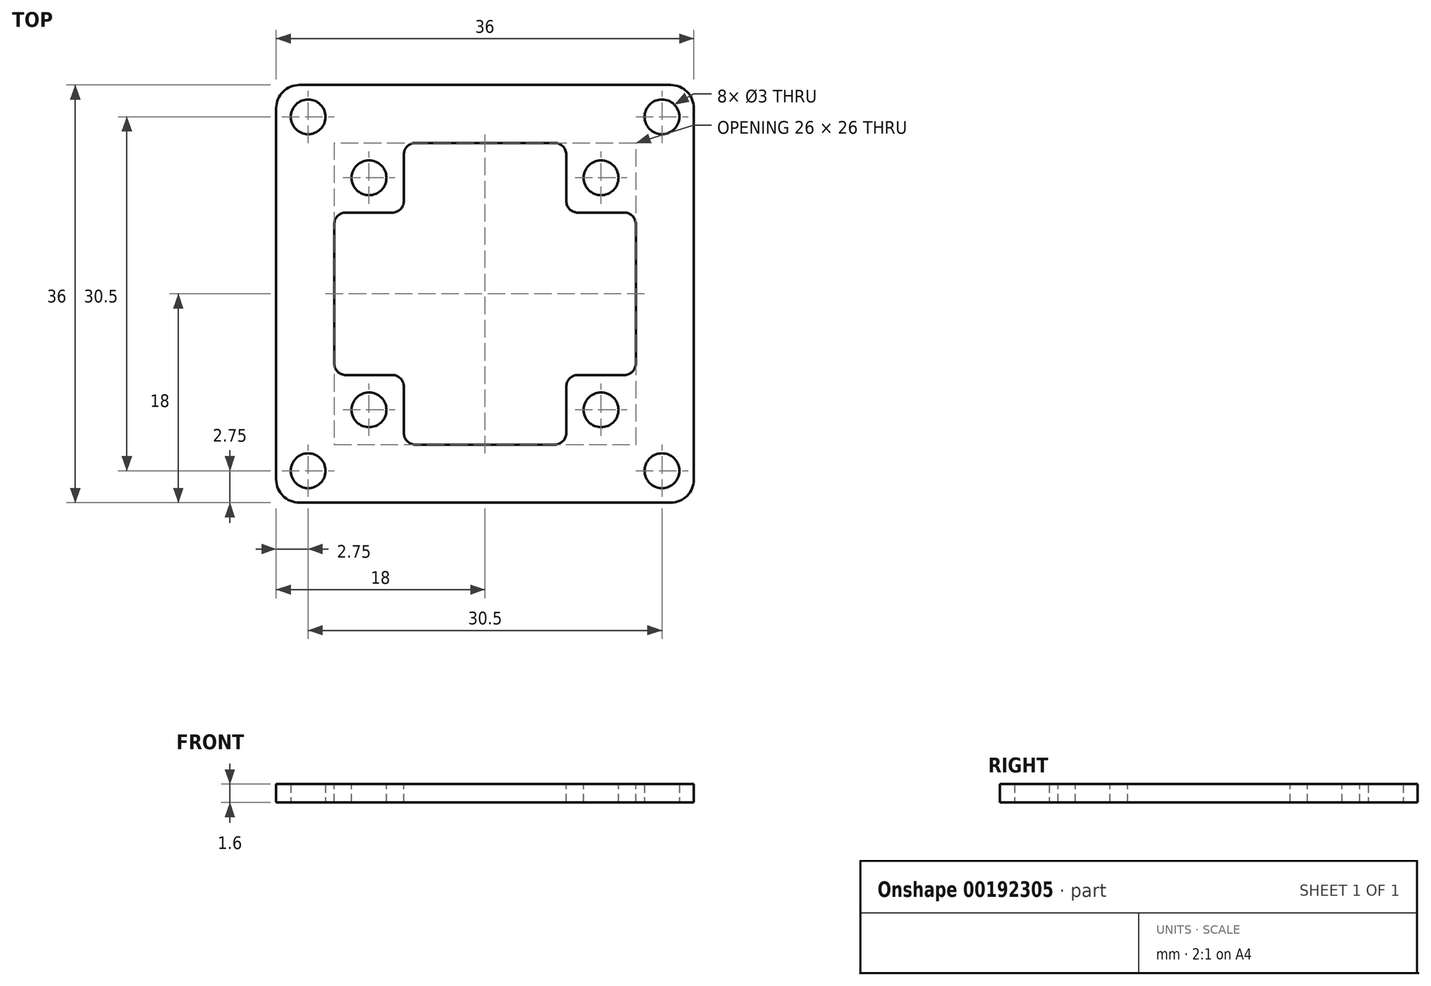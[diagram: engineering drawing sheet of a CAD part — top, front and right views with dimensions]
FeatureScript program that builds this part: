
annotation { "Feature Type Name" : "Feature", "Feature Type Description" : "" }
export const myFeature = defineFeature(function(context is Context, id is Id, definition is map)
    precondition{}
    {
        {
            var Q0;
            Q0=qCreatedBy(makeId("Top.planeOp"),FACE);
            var sketch = newSketch(context, id + "F0", { "sketchPlane" : qUnion([Q0])});
            skLineSegment(sketch, "E0.bottom", {"start": v(0, 0) * mm, "end": v(36, 0) * mm});
            skLineSegment(sketch, "E0.top", {"start": v(0, 36) * mm, "end": v(36, 36) * mm});
            skLineSegment(sketch, "E0.left", {"start": v(0, 0) * mm, "end": v(0, 36) * mm});
            skLineSegment(sketch, "E0.right", {"start": v(36, 0) * mm, "end": v(36, 36) * mm});
            skCircle(sketch, "E1", {"center": v(2.75, 33.25) * mm, "radius": 1.5 * mm});
            skCircle(sketch, "E2", {"center": v(33.25, 33.25) * mm, "radius": 1.5 * mm});
            skCircle(sketch, "E3", {"center": v(33.25, 2.75) * mm, "radius": 1.5 * mm});
            skCircle(sketch, "E4", {"center": v(2.75, 2.75) * mm, "radius": 1.5 * mm});
            skSolve(sketch);
        }
        {
            var Q0;
            Q0=makeQuery(id+"F0.imprint","IMPRINT",FACE,{"disambiguationData":[TD([[makeQuery(id+"F0.imprint","IMPRINT",EDGE,{"derivedFrom":sQuery(id+"F0.wireOp",EDGE,"E0.bottom")}),1.0]])]});
            extrude(context, id + "F1", {"entities" : qUnion([Q0]), "depth" : 1.6 * mm});
        }
        {
            var Q0;
            Q0=makeQuery(id+"F1.opExtrude","SWEPT_EDGE",EDGE,{"disambiguationData":[OSD([sQuery(id+"F0.wireOp",EDGE,"E0.top"),sQuery(id+"F0.wireOp",EDGE,"E0.left")])]});
            var Q1;
            Q1=makeQuery(id+"F1.opExtrude","SWEPT_EDGE",EDGE,{"disambiguationData":[OSD([sQuery(id+"F0.wireOp",EDGE,"E0.top"),sQuery(id+"F0.wireOp",EDGE,"E0.right")])]});
            var Q2;
            Q2=makeQuery(id+"F1.opExtrude","SWEPT_EDGE",EDGE,{"disambiguationData":[OSD([sQuery(id+"F0.wireOp",EDGE,"E0.bottom"),sQuery(id+"F0.wireOp",EDGE,"E0.right")])]});
            var Q3;
            Q3=makeQuery(id+"F1.opExtrude","SWEPT_EDGE",EDGE,{"disambiguationData":[OSD([sQuery(id+"F0.wireOp",EDGE,"E0.bottom"),sQuery(id+"F0.wireOp",EDGE,"E0.left")])]});
            fillet(context, id + "F2", {"entities" : qUnion([Q0, Q1, Q2, Q3]), "radius" : 2 * mm, "tangentPropagation" : true, "allowEdgeOverflow" : false});
        }
        {
            var Q0;
            Q0=makeQuery(id+"F1.opExtrude","CAP_FACE",FACE,{"disambiguationData":[OSD([sQuery(id+"F0.wireOp",EDGE,"E0.bottom"),sQuery(id+"F0.wireOp",EDGE,"E0.top"),sQuery(id+"F0.wireOp",EDGE,"E0.left"),sQuery(id+"F0.wireOp",EDGE,"E0.right"),sQuery(id+"F0.wireOp",EDGE,"E1"),sQuery(id+"F0.wireOp",EDGE,"E2"),sQuery(id+"F0.wireOp",EDGE,"E3"),sQuery(id+"F0.wireOp",EDGE,"E4")])],"isStart":false});
            var sketch = newSketch(context, id + "F3", { "sketchPlane" : qUnion([Q0])});
            skCircle(sketch, "E5", {"center": v(8, 28) * mm, "radius": 1.5 * mm});
            skCircle(sketch, "E6.0.1.0", {"center": v(8, 8) * mm, "radius": 1.5 * mm});
            skCircle(sketch, "E6.1.0.0", {"center": v(28, 28) * mm, "radius": 1.5 * mm});
            skCircle(sketch, "E6.1.1.0", {"center": v(28, 8) * mm, "radius": 1.5 * mm});
            skLineSegment(sketch, "E6.direction1", {"start": v(8, 28) * mm, "end": v(28, 28) * mm, "construction": true});
            skLineSegment(sketch, "E6.direction2", {"start": v(8, 28) * mm, "end": v(8, 8) * mm, "construction": true});
            skSolve(sketch);
        }
        {
            var Q0;
            Q0 = qSketchRegion(id + "F3", true);
            extrude(context, id + "F4", {"entities" : qUnion([Q0]), "operationType" : NewBodyOperationType.REMOVE, "oppositeDirection" : true, "depth" : 25 * mm});
        }
        {
            var Q0;
            Q0=makeQuery(id+"F1.opExtrude","CAP_FACE",FACE,{"disambiguationData":[OSD([sQuery(id+"F0.wireOp",EDGE,"E0.bottom"),sQuery(id+"F0.wireOp",EDGE,"E0.top"),sQuery(id+"F0.wireOp",EDGE,"E0.left"),sQuery(id+"F0.wireOp",EDGE,"E0.right"),sQuery(id+"F0.wireOp",EDGE,"E1"),sQuery(id+"F0.wireOp",EDGE,"E2"),sQuery(id+"F0.wireOp",EDGE,"E3"),sQuery(id+"F0.wireOp",EDGE,"E4")])],"isStart":false});
            var sketch = newSketch(context, id + "F5", { "sketchPlane" : qUnion([Q0])});
            skLineSegment(sketch, "E7.bottom", {"start": v(25, 5) * mm, "end": v(11, 5) * mm});
            skLineSegment(sketch, "E7.top", {"start": v(25, 31) * mm, "end": v(11, 31) * mm});
            skLineSegment(sketch, "E7.left", {"start": v(25, 5) * mm, "end": v(25, 11) * mm});
            skLineSegment(sketch, "E7.right", {"start": v(11, 5) * mm, "end": v(11, 11) * mm});
            skPoint(sketch, "E7.middle", {"position": v(18, 18) * mm});
            skPoint(sketch, "E7.middle.positionSnap0", {"position": v(0, 18) * mm});
            skPoint(sketch, "E7.middle.positionSnap1", {"position": v(18, 0) * mm});
            skPoint(sketch, "E7.centerSnap0", {"position": v(0, 18) * mm});
            skPoint(sketch, "E7.centerSnap1", {"position": v(18, 0) * mm});
            skLineSegment(sketch, "E8.bottom", {"start": v(31, 11) * mm, "end": v(25, 11) * mm});
            skLineSegment(sketch, "E8.top", {"start": v(31, 25) * mm, "end": v(25, 25) * mm});
            skLineSegment(sketch, "E8.left", {"start": v(31, 11) * mm, "end": v(31, 25) * mm});
            skLineSegment(sketch, "E8.right", {"start": v(5, 11) * mm, "end": v(5, 25) * mm});
            skLineSegment(sketch, "E9.trimOffspring", {"start": v(11, 25) * mm, "end": v(5, 25) * mm});
            skLineSegment(sketch, "E10.trimOffspring", {"start": v(11, 25) * mm, "end": v(11, 31) * mm});
            skLineSegment(sketch, "E11.trimOffspring", {"start": v(11, 11) * mm, "end": v(5, 11) * mm});
            skLineSegment(sketch, "E12.trimOffspring", {"start": v(25, 25) * mm, "end": v(25, 31) * mm});
            skSolve(sketch);
        }
        {
            var Q0;
            Q0=makeQuery(id+"F5.imprint","IMPRINT",FACE,{"disambiguationData":[TD([[makeQuery(id+"F5.imprint","IMPRINT",EDGE,{"derivedFrom":sQuery(id+"F5.wireOp",EDGE,"E7.bottom")}),-1.0]])]});
            extrude(context, id + "F6", {"entities" : qUnion([Q0]), "operationType" : NewBodyOperationType.REMOVE, "oppositeDirection" : true, "depth" : 25 * mm});
        }
        {
            var Q0;
            Q0=makeQuery(id+"F6.boolean.opBoolean","COPY",EDGE,{"derivedFrom":makeQuery(id+"F6.opExtrude","SWEPT_EDGE",EDGE,{"disambiguationData":[OSD([sQuery(id+"F5.wireOp",EDGE,"E9.trimOffspring"),sQuery(id+"F5.wireOp",EDGE,"E10.trimOffspring")])]})});
            var Q1;
            Q1=makeQuery(id+"F6.boolean.opBoolean","COPY",EDGE,{"derivedFrom":makeQuery(id+"F6.opExtrude","SWEPT_EDGE",EDGE,{"disambiguationData":[OSD([sQuery(id+"F5.wireOp",EDGE,"E8.top"),sQuery(id+"F5.wireOp",EDGE,"E12.trimOffspring")])]})});
            var Q2;
            Q2=makeQuery(id+"F6.boolean.opBoolean","COPY",EDGE,{"derivedFrom":makeQuery(id+"F6.opExtrude","SWEPT_EDGE",EDGE,{"disambiguationData":[OSD([sQuery(id+"F5.wireOp",EDGE,"E7.left"),sQuery(id+"F5.wireOp",EDGE,"E8.bottom")])]})});
            var Q3;
            Q3=makeQuery(id+"F6.boolean.opBoolean","COPY",EDGE,{"derivedFrom":makeQuery(id+"F6.opExtrude","SWEPT_EDGE",EDGE,{"disambiguationData":[OSD([sQuery(id+"F5.wireOp",EDGE,"E7.right"),sQuery(id+"F5.wireOp",EDGE,"E11.trimOffspring")])]})});
            var Q4;
            Q4=makeQuery(id+"F6.boolean.opBoolean","COPY",EDGE,{"derivedFrom":makeQuery(id+"F6.opExtrude","SWEPT_EDGE",EDGE,{"disambiguationData":[OSD([sQuery(id+"F5.wireOp",EDGE,"E7.bottom"),sQuery(id+"F5.wireOp",EDGE,"E7.right")])]})});
            var Q5;
            Q5=makeQuery(id+"F6.boolean.opBoolean","COPY",EDGE,{"derivedFrom":makeQuery(id+"F6.opExtrude","SWEPT_EDGE",EDGE,{"disambiguationData":[OSD([sQuery(id+"F5.wireOp",EDGE,"E8.right"),sQuery(id+"F5.wireOp",EDGE,"E11.trimOffspring")])]})});
            var Q6;
            Q6=makeQuery(id+"F6.boolean.opBoolean","COPY",EDGE,{"derivedFrom":makeQuery(id+"F6.opExtrude","SWEPT_EDGE",EDGE,{"disambiguationData":[OSD([sQuery(id+"F5.wireOp",EDGE,"E7.bottom"),sQuery(id+"F5.wireOp",EDGE,"E7.left")])]})});
            var Q7;
            Q7=makeQuery(id+"F6.boolean.opBoolean","COPY",EDGE,{"derivedFrom":makeQuery(id+"F6.opExtrude","SWEPT_EDGE",EDGE,{"disambiguationData":[OSD([sQuery(id+"F5.wireOp",EDGE,"E8.bottom"),sQuery(id+"F5.wireOp",EDGE,"E8.left")])]})});
            var Q8;
            Q8=makeQuery(id+"F6.boolean.opBoolean","COPY",EDGE,{"derivedFrom":makeQuery(id+"F6.opExtrude","SWEPT_EDGE",EDGE,{"disambiguationData":[OSD([sQuery(id+"F5.wireOp",EDGE,"E8.right"),sQuery(id+"F5.wireOp",EDGE,"E9.trimOffspring")])]})});
            var Q9;
            Q9=makeQuery(id+"F6.boolean.opBoolean","COPY",EDGE,{"derivedFrom":makeQuery(id+"F6.opExtrude","SWEPT_EDGE",EDGE,{"disambiguationData":[OSD([sQuery(id+"F5.wireOp",EDGE,"E7.top"),sQuery(id+"F5.wireOp",EDGE,"E10.trimOffspring")])]})});
            var Q10;
            Q10=makeQuery(id+"F6.boolean.opBoolean","COPY",EDGE,{"derivedFrom":makeQuery(id+"F6.opExtrude","SWEPT_EDGE",EDGE,{"disambiguationData":[OSD([sQuery(id+"F5.wireOp",EDGE,"E8.top"),sQuery(id+"F5.wireOp",EDGE,"E8.left")])]})});
            var Q11;
            Q11=makeQuery(id+"F6.boolean.opBoolean","COPY",EDGE,{"derivedFrom":makeQuery(id+"F6.opExtrude","SWEPT_EDGE",EDGE,{"disambiguationData":[OSD([sQuery(id+"F5.wireOp",EDGE,"E7.top"),sQuery(id+"F5.wireOp",EDGE,"E12.trimOffspring")])]})});
            fillet(context, id + "F7", {"entities" : qUnion([Q0, Q1, Q2, Q3, Q4, Q5, Q6, Q7, Q8, Q9, Q10, Q11]), "radius" : 1 * mm, "tangentPropagation" : true, "allowEdgeOverflow" : false});
        }
    });
